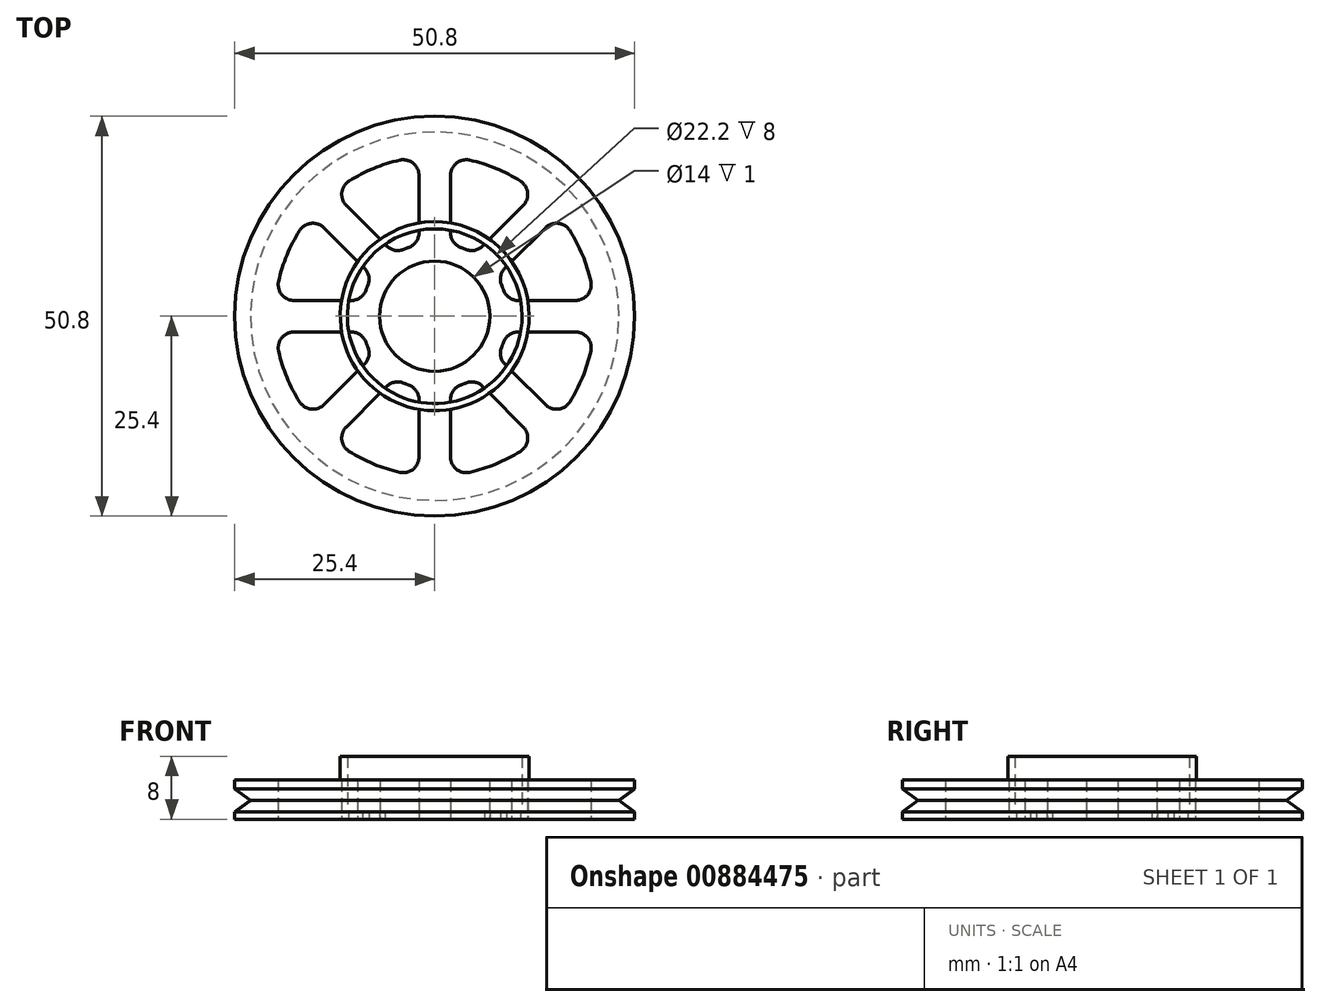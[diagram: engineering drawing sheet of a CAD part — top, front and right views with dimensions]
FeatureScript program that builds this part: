
annotation { "Feature Type Name" : "Feature", "Feature Type Description" : "" }
export const myFeature = defineFeature(function(context is Context, id is Id, definition is map)
    precondition{}
    {
        {
            var Q0;
            Q0=qCreatedBy(makeId("Top.planeOp"),FACE);
            var sketch = newSketch(context, id + "F0", { "sketchPlane" : qUnion([Q0])});
            skCircle(sketch, "E0", {"center": v(0, 0) * mm, "radius": 25.4 * mm});
            skCircle(sketch, "E1", {"center": v(0, 0) * mm, "radius": 3 * mm});
            skArc(sketch, "E2.0", {"start": v(-4.44, 19.83) * mm, "mid": v(-7.78, 18.77) * mm, "end": v(-10.88, 17.16) * mm});
            skArc(sketch, "E3.0", {"start": v(-3.3, 8.75) * mm, "mid": v(-3.58, 8.64) * mm, "end": v(-3.86, 8.52) * mm});
            skLineSegment(sketch, "E4.0", {"start": v(-2, 17.88) * mm, "end": v(-2, 10.62) * mm});
            skLineSegment(sketch, "E5.0", {"start": v(2, 17.88) * mm, "end": v(2, 10.62) * mm});
            skPoint(sketch, "E6.orphan", {"position": v(0, 22.85) * mm});
            skPoint(sketch, "E7.visualSharp", {"position": v(-2, 20.22) * mm});
            skArc(sketch, "E7.filletArc", {"start": v(-2, 17.88) * mm, "mid": v(-2.75, 19.44) * mm, "end": v(-4.44, 19.83) * mm});
            skPoint(sketch, "E8.visualSharp", {"position": v(2, 20.22) * mm});
            skArc(sketch, "E8.filletArc", {"start": v(4.44, 19.83) * mm, "mid": v(2.75, 19.44) * mm, "end": v(2, 17.88) * mm});
            skPoint(sketch, "E9.visualSharp", {"position": v(-2, 9.13) * mm});
            skArc(sketch, "E9.filletArc", {"start": v(-3.3, 8.75) * mm, "mid": v(-2.36, 9.48) * mm, "end": v(-2, 10.62) * mm});
            skPoint(sketch, "E10.visualSharp", {"position": v(2, 9.13) * mm});
            skArc(sketch, "E10.filletArc", {"start": v(2, 10.62) * mm, "mid": v(2.36, 9.48) * mm, "end": v(3.3, 8.75) * mm});
            skArc(sketch, "E11.1.0", {"start": v(-14.06, 11.23) * mm, "mid": v(-15.69, 11.8) * mm, "end": v(-17.16, 10.88) * mm});
            skLineSegment(sketch, "E11.1.1", {"start": v(-14.06, 11.23) * mm, "end": v(-8.92, 6.1) * mm});
            skArc(sketch, "E11.1.2", {"start": v(-8.52, 3.86) * mm, "mid": v(-8.37, 5.04) * mm, "end": v(-8.92, 6.1) * mm});
            skArc(sketch, "E11.1.3", {"start": v(-10.88, 17.16) * mm, "mid": v(-11.8, 15.69) * mm, "end": v(-11.23, 14.06) * mm});
            skLineSegment(sketch, "E11.1.4", {"start": v(-11.23, 14.06) * mm, "end": v(-6.1, 8.92) * mm});
            skArc(sketch, "E11.1.5", {"start": v(-6.1, 8.92) * mm, "mid": v(-5.04, 8.37) * mm, "end": v(-3.86, 8.52) * mm});
            skArc(sketch, "E11.2.0", {"start": v(-17.88, -2) * mm, "mid": v(-19.44, -2.75) * mm, "end": v(-19.83, -4.44) * mm});
            skLineSegment(sketch, "E11.2.1", {"start": v(-17.88, -2) * mm, "end": v(-10.62, -2) * mm});
            skArc(sketch, "E11.2.2", {"start": v(-8.75, -3.3) * mm, "mid": v(-9.48, -2.36) * mm, "end": v(-10.62, -2) * mm});
            skArc(sketch, "E11.2.3", {"start": v(-19.83, 4.44) * mm, "mid": v(-19.44, 2.75) * mm, "end": v(-17.88, 2) * mm});
            skLineSegment(sketch, "E11.2.4", {"start": v(-17.88, 2) * mm, "end": v(-10.62, 2) * mm});
            skArc(sketch, "E11.2.5", {"start": v(-10.62, 2) * mm, "mid": v(-9.48, 2.36) * mm, "end": v(-8.75, 3.3) * mm});
            skArc(sketch, "E11.3.0", {"start": v(-11.23, -14.06) * mm, "mid": v(-11.8, -15.69) * mm, "end": v(-10.88, -17.16) * mm});
            skLineSegment(sketch, "E11.3.1", {"start": v(-11.23, -14.06) * mm, "end": v(-6.1, -8.92) * mm});
            skArc(sketch, "E11.3.2", {"start": v(-3.86, -8.52) * mm, "mid": v(-5.04, -8.37) * mm, "end": v(-6.1, -8.92) * mm});
            skArc(sketch, "E11.3.3", {"start": v(-17.16, -10.88) * mm, "mid": v(-15.69, -11.8) * mm, "end": v(-14.06, -11.23) * mm});
            skLineSegment(sketch, "E11.3.4", {"start": v(-14.06, -11.23) * mm, "end": v(-8.92, -6.1) * mm});
            skArc(sketch, "E11.3.5", {"start": v(-8.92, -6.1) * mm, "mid": v(-8.37, -5.04) * mm, "end": v(-8.52, -3.86) * mm});
            skArc(sketch, "E11.4.0", {"start": v(2, -17.88) * mm, "mid": v(2.75, -19.44) * mm, "end": v(4.44, -19.83) * mm});
            skLineSegment(sketch, "E11.4.1", {"start": v(2, -17.88) * mm, "end": v(2, -10.62) * mm});
            skArc(sketch, "E11.4.2", {"start": v(3.3, -8.75) * mm, "mid": v(2.36, -9.48) * mm, "end": v(2, -10.62) * mm});
            skArc(sketch, "E11.4.3", {"start": v(-4.44, -19.83) * mm, "mid": v(-2.75, -19.44) * mm, "end": v(-2, -17.88) * mm});
            skLineSegment(sketch, "E11.4.4", {"start": v(-2, -17.88) * mm, "end": v(-2, -10.62) * mm});
            skArc(sketch, "E11.4.5", {"start": v(-2, -10.62) * mm, "mid": v(-2.36, -9.48) * mm, "end": v(-3.3, -8.75) * mm});
            skArc(sketch, "E11.5.0", {"start": v(14.06, -11.23) * mm, "mid": v(15.69, -11.8) * mm, "end": v(17.16, -10.88) * mm});
            skLineSegment(sketch, "E11.5.1", {"start": v(14.06, -11.23) * mm, "end": v(8.92, -6.1) * mm});
            skArc(sketch, "E11.5.2", {"start": v(8.52, -3.86) * mm, "mid": v(8.37, -5.04) * mm, "end": v(8.92, -6.1) * mm});
            skArc(sketch, "E11.5.3", {"start": v(10.88, -17.16) * mm, "mid": v(11.8, -15.69) * mm, "end": v(11.23, -14.06) * mm});
            skLineSegment(sketch, "E11.5.4", {"start": v(11.23, -14.06) * mm, "end": v(6.1, -8.92) * mm});
            skArc(sketch, "E11.5.5", {"start": v(6.1, -8.92) * mm, "mid": v(5.04, -8.37) * mm, "end": v(3.86, -8.52) * mm});
            skArc(sketch, "E11.6.0", {"start": v(17.88, 2) * mm, "mid": v(19.44, 2.75) * mm, "end": v(19.83, 4.44) * mm});
            skLineSegment(sketch, "E11.6.1", {"start": v(17.88, 2) * mm, "end": v(10.62, 2) * mm});
            skArc(sketch, "E11.6.2", {"start": v(8.75, 3.3) * mm, "mid": v(9.48, 2.36) * mm, "end": v(10.62, 2) * mm});
            skArc(sketch, "E11.6.3", {"start": v(19.83, -4.44) * mm, "mid": v(19.44, -2.75) * mm, "end": v(17.88, -2) * mm});
            skLineSegment(sketch, "E11.6.4", {"start": v(17.88, -2) * mm, "end": v(10.62, -2) * mm});
            skArc(sketch, "E11.6.5", {"start": v(10.62, -2) * mm, "mid": v(9.48, -2.36) * mm, "end": v(8.75, -3.3) * mm});
            skArc(sketch, "E11.7.0", {"start": v(11.23, 14.06) * mm, "mid": v(11.8, 15.69) * mm, "end": v(10.88, 17.16) * mm});
            skLineSegment(sketch, "E11.7.1", {"start": v(11.23, 14.06) * mm, "end": v(6.1, 8.92) * mm});
            skArc(sketch, "E11.7.2", {"start": v(3.86, 8.52) * mm, "mid": v(5.04, 8.37) * mm, "end": v(6.1, 8.92) * mm});
            skArc(sketch, "E11.7.3", {"start": v(17.16, 10.88) * mm, "mid": v(15.69, 11.8) * mm, "end": v(14.06, 11.23) * mm});
            skLineSegment(sketch, "E11.7.4", {"start": v(14.06, 11.23) * mm, "end": v(8.92, 6.1) * mm});
            skArc(sketch, "E11.7.5", {"start": v(8.92, 6.1) * mm, "mid": v(8.37, 5.04) * mm, "end": v(8.52, 3.86) * mm});
            skArc(sketch, "E12.trimOffspring", {"start": v(-17.16, 10.88) * mm, "mid": v(-18.77, 7.78) * mm, "end": v(-19.83, 4.44) * mm});
            skArc(sketch, "E13.trimOffspring", {"start": v(-8.52, 3.86) * mm, "mid": v(-8.64, 3.58) * mm, "end": v(-8.75, 3.3) * mm});
            skArc(sketch, "E14.trimOffspring", {"start": v(-8.75, -3.3) * mm, "mid": v(-8.64, -3.58) * mm, "end": v(-8.52, -3.86) * mm});
            skArc(sketch, "E15.trimOffspring", {"start": v(-19.83, -4.44) * mm, "mid": v(-18.77, -7.78) * mm, "end": v(-17.16, -10.88) * mm});
            skArc(sketch, "E16.trimOffspring", {"start": v(-10.88, -17.16) * mm, "mid": v(-7.78, -18.77) * mm, "end": v(-4.44, -19.83) * mm});
            skArc(sketch, "E17.trimOffspring", {"start": v(-3.86, -8.52) * mm, "mid": v(-3.58, -8.64) * mm, "end": v(-3.3, -8.75) * mm});
            skArc(sketch, "E18.trimOffspring", {"start": v(3.3, -8.75) * mm, "mid": v(3.58, -8.64) * mm, "end": v(3.86, -8.52) * mm});
            skArc(sketch, "E19.trimOffspring", {"start": v(8.52, -3.86) * mm, "mid": v(8.64, -3.58) * mm, "end": v(8.75, -3.3) * mm});
            skArc(sketch, "E20.trimOffspring", {"start": v(8.75, 3.3) * mm, "mid": v(8.64, 3.58) * mm, "end": v(8.52, 3.86) * mm});
            skArc(sketch, "E21.trimOffspring", {"start": v(3.86, 8.52) * mm, "mid": v(3.58, 8.64) * mm, "end": v(3.3, 8.75) * mm});
            skArc(sketch, "E22.trimOffspring", {"start": v(10.88, 17.16) * mm, "mid": v(7.78, 18.77) * mm, "end": v(4.44, 19.83) * mm});
            skArc(sketch, "E23.trimOffspring", {"start": v(19.83, 4.44) * mm, "mid": v(18.77, 7.78) * mm, "end": v(17.16, 10.88) * mm});
            skArc(sketch, "E24.trimOffspring", {"start": v(17.16, -10.88) * mm, "mid": v(18.77, -7.78) * mm, "end": v(19.83, -4.44) * mm});
            skArc(sketch, "E25.trimOffspring", {"start": v(4.44, -19.83) * mm, "mid": v(7.78, -18.77) * mm, "end": v(10.88, -17.16) * mm});
            skSolve(sketch);
        }
        {
            var Q0;
            Q0=makeQuery(id+"F0.imprint","IMPRINT",FACE,{"disambiguationData":[TD([[makeQuery(id+"F0.imprint","IMPRINT",EDGE,{"derivedFrom":sQuery(id+"F0.wireOp",EDGE,"E0")}),1.0]])]});
            extrude(context, id + "F1", {"entities" : qUnion([Q0]), "depth" : 5 * mm, "offsetDistance" : 25.4 * mm});
        }
        {
            var Q0;
            Q0=qCreatedBy(makeId("Top.planeOp"),FACE);
            var sketch = newSketch(context, id + "F2", { "sketchPlane" : qUnion([Q0])});
            skCircle(sketch, "E26", {"center": v(0, 0) * mm, "radius": 12 * mm});
            skCircle(sketch, "E27", {"center": v(0, 0) * mm, "radius": 11.1 * mm});
            skSolve(sketch);
        }
        {
            var Q0;
            Q0=makeQuery(id+"F2.imprint","IMPRINT",FACE,{"disambiguationData":[TD([[makeQuery(id+"F2.imprint","IMPRINT",EDGE,{"derivedFrom":sQuery(id+"F2.wireOp",EDGE,"E26")}),1.0]])]});
            extrude(context, id + "F3", {"entities" : qUnion([Q0]), "operationType" : NewBodyOperationType.ADD, "depth" : 8 * mm, "offsetDistance" : 25.4 * mm});
        }
        {
            var Q0;
            Q0=makeQuery(id+"F3.opExtrude","CAP_FACE",FACE,{"disambiguationData":[OSD([sQuery(id+"F2.wireOp",EDGE,"E26")])],"isStart":false});
            var sketch = newSketch(context, id + "F4", { "sketchPlane" : qUnion([Q0])});
            skCircle(sketch, "E28", {"center": v(0, 0) * mm, "radius": 3 * mm});
            skSolve(sketch);
        }
        {
            var Q0;
            Q0=makeQuery(id+"F4.imprint","IMPRINT",FACE,{"disambiguationData":[TD([[makeQuery(id+"F4.imprint","IMPRINT",EDGE,{"derivedFrom":sQuery(id+"F4.wireOp",EDGE,"E28")}),1.0]])]});
            extrude(context, id + "F5", {"entities" : qUnion([Q0]), "operationType" : NewBodyOperationType.REMOVE, "endBound" : BoundingType.THROUGH_ALL, "oppositeDirection" : true, "depth" : 25.4 * mm, "offsetDistance" : 25.4 * mm});
        }
        {
            var Q0;
            Q0=qCreatedBy(makeId("Right.planeOp"),FACE);
            var sketch = newSketch(context, id + "F6", { "sketchPlane" : qUnion([Q0])});
            skLineSegment(sketch, "E29", {"start": v(25.4, 2.4) * mm, "end": v(23.4, 2.4) * mm});
            skLineSegment(sketch, "E30", {"start": v(23.4, 2.4) * mm, "end": v(25.46, 3.9) * mm});
            skLineSegment(sketch, "E31", {"start": v(25.46, 3.9) * mm, "end": v(25.4, 2.4) * mm});
            skLineSegment(sketch, "E32.MirrorCS", {"start": v(23.4, 2.4) * mm, "end": v(25.46, 0.9) * mm});
            skLineSegment(sketch, "E33.MirrorCS", {"start": v(25.46, 0.9) * mm, "end": v(25.4, 2.4) * mm});
            skLineSegment(sketch, "E34", {"start": v(0, 19.4) * mm, "end": v(0, -3.2) * mm, "construction": true});
            skSolve(sketch);
        }
        {
            var Q0;
            Q0=qSketchRegion(id+"F6",true);
            var Q1;
            Q1=sQuery(id+"F6.wireOp",EDGE,"E34");
            revolve(context, id + "F7", {"operationType" : NewBodyOperationType.REMOVE, "surfaceOperationType" : NewSurfaceOperationType.NEW, "entities" : qUnion([Q0]), "axis" : qUnion([Q1]), "revolveType" : RevolveType.FULL, "oppositeDirection" : true});
        }
        {
            var Q0;
            Q0=qCreatedBy(makeId("Top.planeOp"),FACE);
            var sketch = newSketch(context, id + "F8", { "sketchPlane" : qUnion([Q0])});
            skCircle(sketch, "E35", {"center": v(0, 0) * mm, "radius": 7 * mm});
            skCircle(sketch, "E36.0", {"center": v(0, 0) * mm, "radius": 10.05 * mm});
            skSolve(sketch);
        }
        {
            var Q0;
            {var subQ0=sQuery(id+"F0.wireOp",EDGE,"E11.4.5");var subQ1=sQuery(id+"F0.wireOp",EDGE,"E11.4.2");var subQ2=sQuery(id+"F0.wireOp",EDGE,"E11.4.1");var subQ3=sQuery(id+"F0.wireOp",EDGE,"E11.3.1");var subQ4=sQuery(id+"F0.wireOp",EDGE,"E11.2.5");var subQ5=sQuery(id+"F0.wireOp",EDGE,"E11.2.4");var subQ6=sQuery(id+"F0.wireOp",EDGE,"E11.2.2");var subQ7=sQuery(id+"F0.wireOp",EDGE,"E11.2.1");var subQ8=sQuery(id+"F0.wireOp",EDGE,"E5.0");var subQ9=sQuery(id+"F0.wireOp",EDGE,"E11.3.5");var subQ10=sQuery(id+"F0.wireOp",EDGE,"E4.0");var subQ11=sQuery(id+"F0.wireOp",EDGE,"E11.7.5");var subQ12=sQuery(id+"F0.wireOp",EDGE,"E11.1.5");var subQ13=sQuery(id+"F0.wireOp",EDGE,"E11.3.4");var subQ14=sQuery(id+"F0.wireOp",EDGE,"E3.0");var subQ15=sQuery(id+"F0.wireOp",EDGE,"E11.7.4");var subQ16=sQuery(id+"F0.wireOp",EDGE,"E11.1.4");var subQ17=sQuery(id+"F0.wireOp",EDGE,"E21.trimOffspring");var subQ18=sQuery(id+"F0.wireOp",EDGE,"E11.3.2");var subQ19=sQuery(id+"F0.wireOp",EDGE,"E1");var subQ20=sQuery(id+"F0.wireOp",EDGE,"E11.7.2");var subQ21=sQuery(id+"F0.wireOp",EDGE,"E11.1.2");var subQ22=sQuery(id+"F0.wireOp",EDGE,"E19.trimOffspring");var subQ23=sQuery(id+"F0.wireOp",EDGE,"E9.filletArc");var subQ24=sQuery(id+"F0.wireOp",EDGE,"E11.4.4");var subQ25=sQuery(id+"F0.wireOp",EDGE,"E10.filletArc");var subQ26=sQuery(id+"F0.wireOp",EDGE,"E11.1.1");var subQ27=sQuery(id+"F0.wireOp",EDGE,"E18.trimOffspring");var subQ28=sQuery(id+"F0.wireOp",EDGE,"E11.5.1");var subQ29=sQuery(id+"F0.wireOp",EDGE,"E11.5.2");var subQ30=sQuery(id+"F0.wireOp",EDGE,"E11.5.4");var subQ31=sQuery(id+"F0.wireOp",EDGE,"E11.5.5");var subQ32=sQuery(id+"F0.wireOp",EDGE,"E11.6.1");var subQ33=sQuery(id+"F0.wireOp",EDGE,"E11.6.2");var subQ34=sQuery(id+"F0.wireOp",EDGE,"E11.6.4");var subQ35=sQuery(id+"F0.wireOp",EDGE,"E11.6.5");var subQ36=sQuery(id+"F0.wireOp",EDGE,"E11.7.1");var subQ37=sQuery(id+"F0.wireOp",EDGE,"E13.trimOffspring");var subQ38=sQuery(id+"F0.wireOp",EDGE,"E14.trimOffspring");var subQ39=sQuery(id+"F0.wireOp",EDGE,"E17.trimOffspring");var subQ40=sQuery(id+"F0.wireOp",EDGE,"E20.trimOffspring");Q0=makeQuery(id+"F3.boolean.opBoolean","SPLIT",FACE,{"disambiguationData":[TD([makeQuery(id+"F1.opExtrude","SWEPT_FACE",FACE,{"disambiguationData":[OSD([subQ19])]})])],"derivedFrom":makeQuery(id+"F1.opExtrude","CAP_FACE",FACE,{"disambiguationData":[OSD([sQuery(id+"F0.wireOp",EDGE,"E0"),subQ19,sQuery(id+"F0.wireOp",EDGE,"E2.0"),subQ14,subQ10,subQ8,sQuery(id+"F0.wireOp",EDGE,"E7.filletArc"),sQuery(id+"F0.wireOp",EDGE,"E8.filletArc"),subQ23,subQ25,sQuery(id+"F0.wireOp",EDGE,"E11.1.0"),subQ26,subQ21,sQuery(id+"F0.wireOp",EDGE,"E11.1.3"),subQ16,subQ12,sQuery(id+"F0.wireOp",EDGE,"E11.2.0"),subQ7,subQ6,sQuery(id+"F0.wireOp",EDGE,"E11.2.3"),subQ5,subQ4,sQuery(id+"F0.wireOp",EDGE,"E11.3.0"),subQ3,subQ18,sQuery(id+"F0.wireOp",EDGE,"E11.3.3"),subQ13,subQ9,sQuery(id+"F0.wireOp",EDGE,"E11.4.0"),subQ2,subQ1,sQuery(id+"F0.wireOp",EDGE,"E11.4.3"),subQ24,subQ0,sQuery(id+"F0.wireOp",EDGE,"E11.5.0"),subQ28,subQ29,sQuery(id+"F0.wireOp",EDGE,"E11.5.3"),subQ30,subQ31,sQuery(id+"F0.wireOp",EDGE,"E11.6.0"),subQ32,subQ33,sQuery(id+"F0.wireOp",EDGE,"E11.6.3"),subQ34,subQ35,sQuery(id+"F0.wireOp",EDGE,"E11.7.0"),subQ36,subQ20,sQuery(id+"F0.wireOp",EDGE,"E11.7.3"),subQ15,subQ11,sQuery(id+"F0.wireOp",EDGE,"E12.trimOffspring"),subQ37,subQ38,sQuery(id+"F0.wireOp",EDGE,"E15.trimOffspring"),sQuery(id+"F0.wireOp",EDGE,"E16.trimOffspring"),subQ39,subQ27,subQ22,subQ40,subQ17,sQuery(id+"F0.wireOp",EDGE,"E22.trimOffspring"),sQuery(id+"F0.wireOp",EDGE,"E23.trimOffspring"),sQuery(id+"F0.wireOp",EDGE,"E24.trimOffspring"),sQuery(id+"F0.wireOp",EDGE,"E25.trimOffspring")])],"isStart":false})});}
            extrude(context, id + "F9", {"entities" : qUnion([Q0]), "operationType" : NewBodyOperationType.REMOVE, "oppositeDirection" : true, "depth" : 4 * mm, "offsetDistance" : 25.4 * mm});
        }
        {
            var Q0;
            Q0=makeQuery(id+"F8.imprint","IMPRINT",FACE,{"disambiguationData":[TD([[makeQuery(id+"F8.imprint","IMPRINT",EDGE,{"derivedFrom":sQuery(id+"F8.wireOp",EDGE,"E35")}),1.0]])]});
            extrude(context, id + "F10", {"entities" : qUnion([Q0]), "operationType" : NewBodyOperationType.REMOVE, "endBound" : BoundingType.THROUGH_ALL, "depth" : 25.4 * mm, "offsetDistance" : 25.4 * mm});
        }
    });
